# Revit family: 230688WCG01-011-WMMS3330R_230688WCG01-011-WMMS3330RZV
name_source: partatom
category: Specialty Equipment
units: mm (PartAtom-declared; Revit-internal decimal feet)

## family parameters
Always vertical = Yes
Cut with Voids When Loaded = No
Enable Cutting in Views = No
Maintain Annotation Orientation = No
Part Type = Normal
Room Calculation Point = No
Round Connector Dimension = Use Diameter
Shared = No
Work Plane-Based = No

## types (2) — shared parameters
Accent Material = ARCAT - Metal - Steel - Gray - Light
Apparent Load = 15 VA
Back Panel = ARCAT - Metal - Steel - Grey
Body Material = ARCAT - Metal - Steel - Black Stainless
Clearance Material = ARCAT - Clearance
Default Elevation = 0"
Depth = 15 9/16"
Description = 30’ W 1.9 cu. ft Over the range Microwave with Sensor Cooking
Dimension Guide = https://www.whirlpool.com
Display Panel Material = ARCAT - Glass - Black
Display Unit = ARCAT - Metal - Steel - Black Stainless
Door Frame = ARCAT - Metal - Steel - Black Stainless
Energy Guide = N/A (we do not create energy guides for MHCs)
Family Name = Titan
Feature 1 = Sensor Cooking
Feature 2 = Express Cooking Buttons
Feature 3 = Microwave Presets
Glass Material = ARCAT - Glass - Tempered - Black
Height = 17 1/8"
Hz = 60 Hz
Installation-Fabrication = https://www.whirlpool.com
Ring = ARCAT - Metal - Steel - Red
Style Master = ARCAT - Metal - Steel - Stainless - Light
Voltage = 120 V
Width = 29 7/8"

## per-type parameters (varying)
| type | Door Front Panel Material | Door Material |
| WMMS3330RZ | ARCAT - Metal - Steel - Stainless | ARCAT - Metal - Steel - Stainless(2) |
| WMMS3330RV | ARCAT - Metal - Steel - Black(1) | ARCAT - Metal - Steel - Stainless(1) |

## geometry (parser evidence)
native form markers: Sweep x7
no freeform markers — native parametric forms only
